# Revit family: SNS Merlin Carbon Dioxide Detector TFT
name_source: partatom
category: Electrical Equipment
units: mm (PartAtom-declared; Revit-internal decimal feet)

## family parameters
Always vertical = Yes
Cut with Voids When Loaded = No
OmniClass Number = 23.80.30.11.17
OmniClass Title = Distribution Boards and Control Panels
Part Type = Other Panel
Room Calculation Point = No
Round Connector Dimension = Use Diameter
Shared = No
Work Plane-Based = No

## types (1)
- SNS Merlin CO TFT Gas Detector
    Default Height = 4' - 0"
    Description = The Merlin CO2-X Monitor features a TFT display to show the user a clear precise reading of the CO2 level in the room and also uses a traffic light colour system to indicate whether the air quality in the room is at a safe, adequate or dangerous level.
The Merlin CO2-X can be used independently or can work in conjunction with one of our Merlin gas safety systems. In the event where the CO2 levels rose to a dangerous level the Merlin CO2-X Monitor will sound an audible alarm to alert the user of the danger, automatically drive ventilation fans reducing CO2 & temperature as well as shutting off any connected utilities such as gas solenoid valves or relays to boilers.
    Load = 120 VA
    Manufacturer = S&S Northern Ltd.
    Model = SNS Merlin CO TFT Gas Detector
    Product Information = https://snsnorthern.com
    Type Comments = The Merlin CO2-X Monitor features a TFT display to show the user a clear precise reading of the CO2 level in the room and also uses a traffic light colour system to indicate whether the air quality in the room is at a safe, adequate or dangerous level.
The Merlin CO2-X can be used independently or can work in conjunction with one of our Merlin gas safety systems. In the event where the CO2 levels rose to a dangerous level the Merlin CO2-X Monitor will sound an audible alarm to alert the user of the danger, automatically drive ventilation fans reducing CO2 & temperature as well as shutting off any connected utilities such as gas solenoid valves or relays to boilers.
    URL = https://snsnorthern.com
    Voltage = 120VAC

## geometry (parser evidence)
native form markers: Sweep x14
no freeform markers — native parametric forms only
